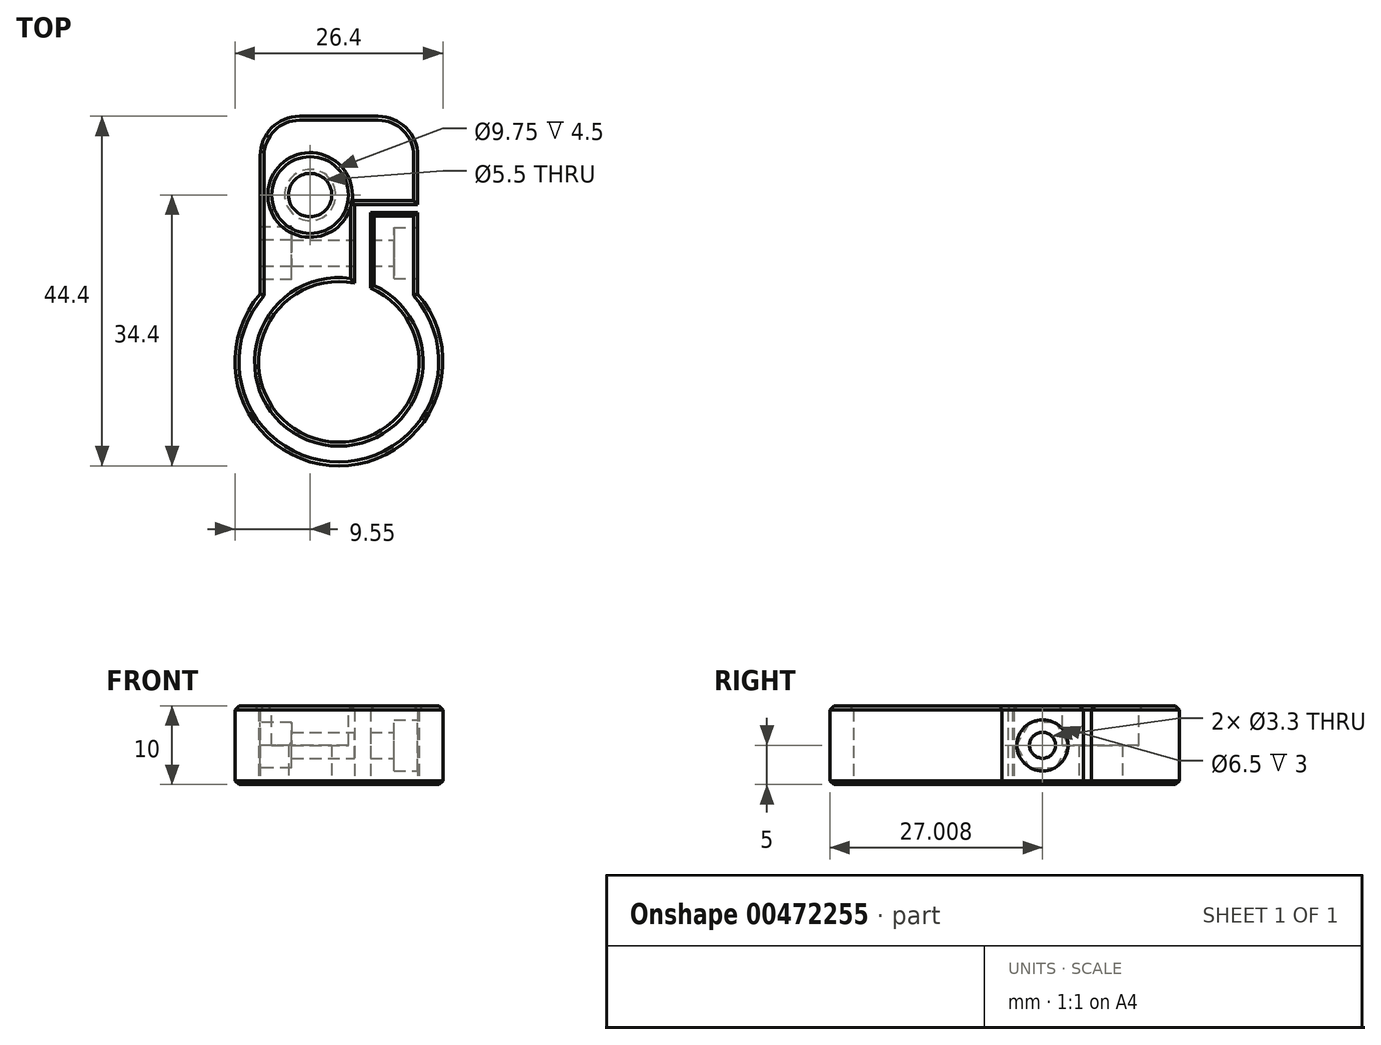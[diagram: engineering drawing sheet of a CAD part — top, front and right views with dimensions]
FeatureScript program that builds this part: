
annotation { "Feature Type Name" : "Feature", "Feature Type Description" : "" }
export const myFeature = defineFeature(function(context is Context, id is Id, definition is map)
    precondition{}
    {
        {
            var Q0;
            Q0=qCreatedBy(makeId("Top.planeOp"),FACE);
            var sketch = newSketch(context, id + "F0", { "sketchPlane" : qUnion([Q0])});
            skArc(sketch, "E0", {"start": v(2, -1.2) * mm, "mid": v(-3.02, -20.94) * mm, "end": v(4, -1.82) * mm});
            skArc(sketch, "E1.0", {"start": v(-10, -2.58) * mm, "mid": v(0, -24.4) * mm, "end": v(10, -2.58) * mm});
            skLineSegment(sketch, "E2.bottom", {"start": v(-10, 20) * mm, "end": v(10, 20) * mm});
            skLineSegment(sketch, "E2.left", {"start": v(-10, 20) * mm, "end": v(-10, -2.58) * mm});
            skLineSegment(sketch, "E2.right", {"start": v(10, 20) * mm, "end": v(10, 8.8) * mm});
            skLineSegment(sketch, "E3", {"start": v(4, -1.82) * mm, "end": v(4, 7.8) * mm});
            skLineSegment(sketch, "E4", {"start": v(4, 7.8) * mm, "end": v(10, 7.8) * mm});
            skLineSegment(sketch, "E5", {"start": v(10, 8.8) * mm, "end": v(2, 8.8) * mm});
            skLineSegment(sketch, "E6", {"start": v(2, 8.8) * mm, "end": v(2, -1.2) * mm});
            skLineSegment(sketch, "E7", {"start": v(-10.87, 1.8) * mm, "end": v(11.83, 1.8) * mm, "construction": true});
            skLineSegment(sketch, "E8", {"start": v(-10, 10) * mm, "end": v(10, 10) * mm, "construction": true});
            skCircle(sketch, "E9", {"center": v(-3.65, 10) * mm, "radius": 2.75 * mm});
            skLineSegment(sketch, "E10.trimOffspring", {"start": v(10, 7.8) * mm, "end": v(10, -2.58) * mm});
            skSolve(sketch);
        }
        {
            var Q0;
            Q0=makeQuery(id+"F0.imprint","IMPRINT",FACE,{"disambiguationData":[TD([[makeQuery(id+"F0.imprint","IMPRINT",EDGE,{"derivedFrom":sQuery(id+"F0.wireOp",EDGE,"E0")}),-1.0]])]});
            extrude(context, id + "F1", {"entities" : qUnion([Q0]), "depth" : 10 * mm});
        }
        {
            var Q0;
            Q0=makeQuery(id+"F1.opExtrude","CAP_FACE",FACE,{"disambiguationData":[OSD([sQuery(id+"F0.wireOp",EDGE,"E0"),sQuery(id+"F0.wireOp",EDGE,"E1.0"),sQuery(id+"F0.wireOp",EDGE,"E2.bottom"),sQuery(id+"F0.wireOp",EDGE,"E2.left"),sQuery(id+"F0.wireOp",EDGE,"E2.right"),sQuery(id+"F0.wireOp",EDGE,"E3"),sQuery(id+"F0.wireOp",EDGE,"E4"),sQuery(id+"F0.wireOp",EDGE,"E5"),sQuery(id+"F0.wireOp",EDGE,"E6"),sQuery(id+"F0.wireOp",EDGE,"E9"),sQuery(id+"F0.wireOp",EDGE,"E10.trimOffspring")])],"isStart":false});
            var sketch = newSketch(context, id + "F2", { "sketchPlane" : qUnion([Q0])});
            skPoint(sketch, "E11", {"position": v(-3.65, 10) * mm});
            skSolve(sketch);
        }
        {
            var Q0;
            Q0=sQuery(id+"F2.wireOp",VERTEX,"E11");
            var Q1;
            Q1=makeQuery(id+"F1.opExtrude","SWEPT_BODY",BODY,{"disambiguationData":[OSD([sQuery(id+"F0.wireOp",EDGE,"E0"),sQuery(id+"F0.wireOp",EDGE,"E1.0"),sQuery(id+"F0.wireOp",EDGE,"E2.bottom"),sQuery(id+"F0.wireOp",EDGE,"E2.left"),sQuery(id+"F0.wireOp",EDGE,"E2.right"),sQuery(id+"F0.wireOp",EDGE,"E3"),sQuery(id+"F0.wireOp",EDGE,"E4"),sQuery(id+"F0.wireOp",EDGE,"E5"),sQuery(id+"F0.wireOp",EDGE,"E6"),sQuery(id+"F0.wireOp",EDGE,"E9"),sQuery(id+"F0.wireOp",EDGE,"E10.trimOffspring")])]});
            hole(context, id + "F3", {"style" : HoleStyle.C_BORE, "endStyle" : HoleEndStyle.BLIND, "standardTappedOrClearance" : lookupTablePath({ "standard" : "ISO", "fit" : "Normal", "size" : "M5", "type" : "Clearance" }), "standardBlindInLast" : lookupTablePath({ "fit" : "Standard", "standard" : "ISO", "size" : "M5", "type" : "Clearance" }), "holeDiameter" : 5.5 * mm, "cBoreDiameter" : 9.75 * mm, "cBoreDepth" : 5 * mm, "holeDepth" : (25 - 1.5) * mm, "isTappedThrough" : true, "tappedDepth" : 15 * mm, "tapClearance" : 0, "locations" : qUnion([Q0]), "scope" : qUnion([Q1])});
        }
        {
            var Q0;
            Q0=makeQuery(id+"F1.opExtrude","SWEPT_FACE",FACE,{"disambiguationData":[OSD([sQuery(id+"F0.wireOp",EDGE,"E10.trimOffspring")])]});
            var sketch = newSketch(context, id + "F4", { "sketchPlane" : qUnion([Q0])});
            skLineSegment(sketch, "E12", {"start": v(-2.58, 5) * mm, "end": v(7.8, 5) * mm, "construction": true});
            skPoint(sketch, "E13", {"position": v(2.6, 5) * mm});
            skSolve(sketch);
        }
        {
            var Q0;
            Q0=sQuery(id+"F4.wireOp",VERTEX,"E13");
            var Q1;
            Q1=makeQuery(id+"F1.opExtrude","SWEPT_BODY",BODY,{"disambiguationData":[OSD([sQuery(id+"F0.wireOp",EDGE,"E0"),sQuery(id+"F0.wireOp",EDGE,"E1.0"),sQuery(id+"F0.wireOp",EDGE,"E2.bottom"),sQuery(id+"F0.wireOp",EDGE,"E2.left"),sQuery(id+"F0.wireOp",EDGE,"E2.right"),sQuery(id+"F0.wireOp",EDGE,"E3"),sQuery(id+"F0.wireOp",EDGE,"E4"),sQuery(id+"F0.wireOp",EDGE,"E5"),sQuery(id+"F0.wireOp",EDGE,"E6"),sQuery(id+"F0.wireOp",EDGE,"E9"),sQuery(id+"F0.wireOp",EDGE,"E10.trimOffspring")])]});
            hole(context, id + "F5", {"style" : HoleStyle.C_BORE, "endStyle" : HoleEndStyle.BLIND, "standardTappedOrClearance" : lookupTablePath({ "standard" : "ISO", "fit" : "Normal", "size" : "M3", "type" : "Clearance" }), "standardBlindInLast" : lookupTablePath({ "fit" : "Standard", "standard" : "ISO", "size" : "M3", "type" : "Clearance" }), "holeDiameter" : 3.3 * mm, "cBoreDiameter" : 6.5 * mm, "cBoreDepth" : 3 * mm, "holeDepth" : 20 * mm, "isTappedThrough" : true, "tappedDepth" : 15 * mm, "tapClearance" : 0, "locations" : qUnion([Q0]), "scope" : qUnion([Q1])});
        }
        {
            var Q0;
            Q0=makeQuery(id+"F1.opExtrude","SWEPT_FACE",FACE,{"disambiguationData":[OSD([sQuery(id+"F0.wireOp",EDGE,"E2.left")])]});
            var sketch = newSketch(context, id + "F6", { "sketchPlane" : qUnion([Q0])});
            skCircle(sketch, "E14.cCircle", {"center": v(-2.6, 5) * mm, "radius": 2.9 * mm, "construction": true});
            skLineSegment(sketch, "E14.0", {"start": v(-4.28, 2.1) * mm, "end": v(-5.96, 5) * mm});
            skLineSegment(sketch, "E14.1", {"start": v(-5.96, 5) * mm, "end": v(-4.28, 7.9) * mm});
            skLineSegment(sketch, "E14.2", {"start": v(-4.28, 7.9) * mm, "end": v(-0.93, 7.9) * mm});
            skLineSegment(sketch, "E14.3", {"start": v(-0.93, 7.9) * mm, "end": v(0.74, 5) * mm});
            skLineSegment(sketch, "E14.4", {"start": v(0.74, 5) * mm, "end": v(-0.93, 2.1) * mm});
            skLineSegment(sketch, "E14.5", {"start": v(-0.93, 2.1) * mm, "end": v(-4.28, 2.1) * mm});
            skPoint(sketch, "E14.0.midPoint", {"position": v(-5.12, 3.55) * mm});
            skSolve(sketch);
        }
        {
            var Q0;
            Q0=makeQuery(id+"F6.imprint","IMPRINT",FACE,{"disambiguationData":[TD([[makeQuery(id+"F6.imprint","IMPRINT",EDGE,{"derivedFrom":sQuery(id+"F6.wireOp",EDGE,"E14.0")}),-1.0]])]});
            extrude(context, id + "F7", {"entities" : qUnion([Q0]), "operationType" : NewBodyOperationType.REMOVE, "oppositeDirection" : true, "depth" : 4 * mm});
        }
        {
            var Q0;
            Q0=makeQuery(id+"F1.opExtrude","SWEPT_EDGE",EDGE,{"disambiguationData":[OSD([sQuery(id+"F0.wireOp",EDGE,"E2.bottom"),sQuery(id+"F0.wireOp",EDGE,"E2.right")])]});
            var Q1;
            Q1=makeQuery(id+"F1.opExtrude","SWEPT_EDGE",EDGE,{"disambiguationData":[OSD([sQuery(id+"F0.wireOp",EDGE,"E2.bottom"),sQuery(id+"F0.wireOp",EDGE,"E2.left")])]});
            fillet(context, id + "F8", {"entities" : qUnion([Q0, Q1]), "radius" : 5 * mm, "tangentPropagation" : true, "allowEdgeOverflow" : false});
        }
        {
            var Q0;
            Q0=makeQuery(id+"F1.opExtrude","CAP_FACE",FACE,{"disambiguationData":[OSD([sQuery(id+"F0.wireOp",EDGE,"E0"),sQuery(id+"F0.wireOp",EDGE,"E1.0"),sQuery(id+"F0.wireOp",EDGE,"E2.bottom"),sQuery(id+"F0.wireOp",EDGE,"E2.left"),sQuery(id+"F0.wireOp",EDGE,"E2.right"),sQuery(id+"F0.wireOp",EDGE,"E3"),sQuery(id+"F0.wireOp",EDGE,"E4"),sQuery(id+"F0.wireOp",EDGE,"E5"),sQuery(id+"F0.wireOp",EDGE,"E6"),sQuery(id+"F0.wireOp",EDGE,"E9"),sQuery(id+"F0.wireOp",EDGE,"E10.trimOffspring")])],"isStart":false});
            var Q1;
            Q1=makeQuery(id+"F1.opExtrude","CAP_FACE",FACE,{"disambiguationData":[OSD([sQuery(id+"F0.wireOp",EDGE,"E0"),sQuery(id+"F0.wireOp",EDGE,"E1.0"),sQuery(id+"F0.wireOp",EDGE,"E2.bottom"),sQuery(id+"F0.wireOp",EDGE,"E2.left"),sQuery(id+"F0.wireOp",EDGE,"E2.right"),sQuery(id+"F0.wireOp",EDGE,"E3"),sQuery(id+"F0.wireOp",EDGE,"E4"),sQuery(id+"F0.wireOp",EDGE,"E5"),sQuery(id+"F0.wireOp",EDGE,"E6"),sQuery(id+"F0.wireOp",EDGE,"E9"),sQuery(id+"F0.wireOp",EDGE,"E10.trimOffspring")])],"isStart":true});
            chamfer(context, id + "F9", {"entities" : qUnion([Q0, Q1]), "width" : .5 * mm, "tangentPropagation" : true});
        }
    });
